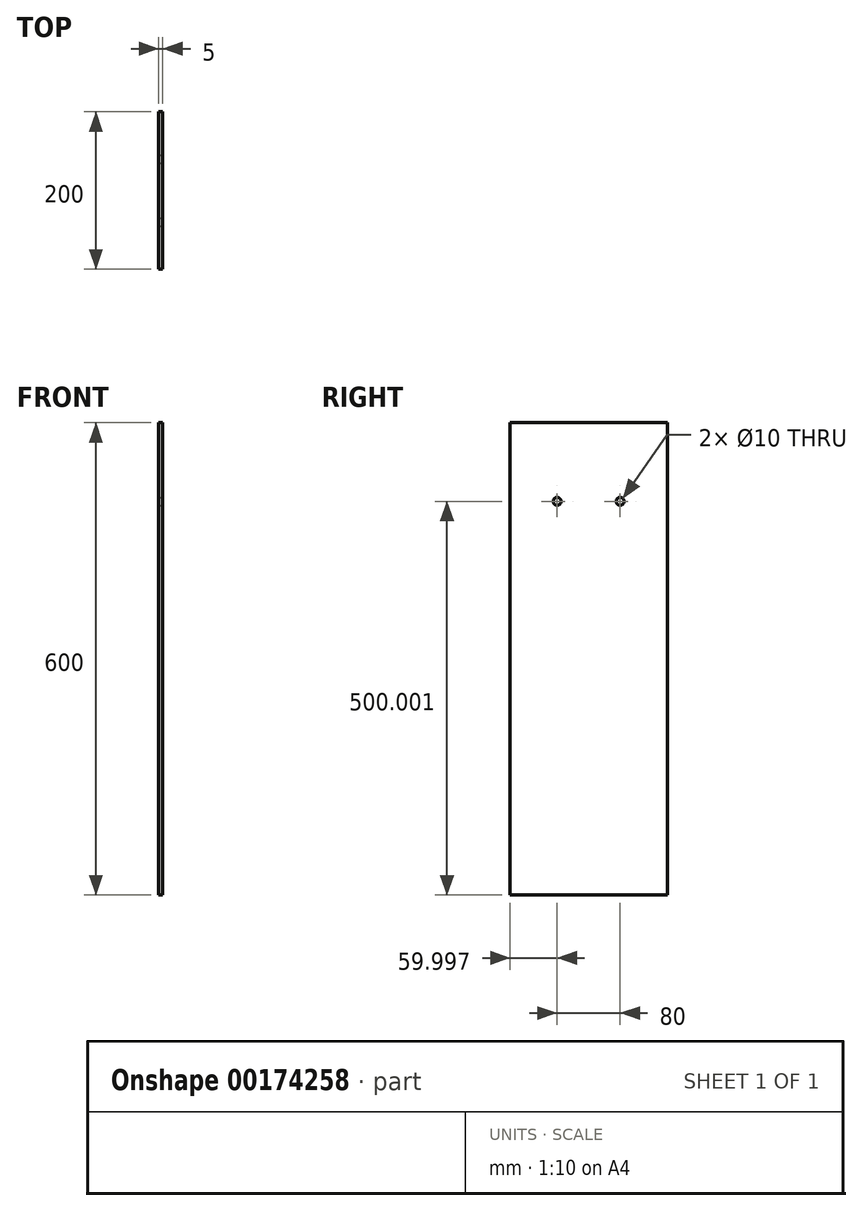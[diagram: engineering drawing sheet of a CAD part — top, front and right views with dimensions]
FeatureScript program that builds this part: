
annotation { "Feature Type Name" : "Feature", "Feature Type Description" : "" }
export const myFeature = defineFeature(function(context is Context, id is Id, definition is map)
    precondition{}
    {
        {
            var Q0;
            Q0=qCreatedBy(makeId("Right.planeOp"),FACE);
            var sketch = newSketch(context, id + "F0", { "sketchPlane" : qUnion([Q0])});
            skLineSegment(sketch, "E0.bottom", {"start": v(95.7, 383.9) * mm, "end": v(-104.3, 383.9) * mm});
            skLineSegment(sketch, "E0.top", {"start": v(95.7, -216.1) * mm, "end": v(-104.3, -216.1) * mm});
            skLineSegment(sketch, "E0.left", {"start": v(95.7, 383.9) * mm, "end": v(95.7, -216.1) * mm});
            skLineSegment(sketch, "E0.right", {"start": v(-104.3, 383.9) * mm, "end": v(-104.3, -216.1) * mm});
            skSolve(sketch);
        }
        {
            var Q0;
            Q0=makeQuery(id+"F0.imprint","IMPRINT",FACE,{"disambiguationData":[TD([[makeQuery(id+"F0.imprint","IMPRINT",EDGE,{"derivedFrom":sQuery(id+"F0.wireOp",EDGE,"E0.bottom")}),1.0]])]});
            extrude(context, id + "F1", {"entities" : qUnion([Q0]), "depth" : 5 * mm});
        }
        {
            var Q0;
            Q0=makeQuery(id+"F1.opExtrude","CAP_FACE",FACE,{"disambiguationData":[OSD([sQuery(id+"F0.wireOp",EDGE,"E0.bottom"),sQuery(id+"F0.wireOp",EDGE,"E0.top"),sQuery(id+"F0.wireOp",EDGE,"E0.left"),sQuery(id+"F0.wireOp",EDGE,"E0.right")])],"isStart":false});
            var sketch = newSketch(context, id + "F2", { "sketchPlane" : qUnion([Q0])});
            skSolve(sketch);
        }
        {
            var Q0;
            Q0=makeQuery(id+"F2.imprint","IMPRINT",FACE,{"disambiguationData":[TD([[makeQuery(id+"F2.imprint","IMPRINT",EDGE,{"derivedFrom":makeQuery(id+"F1.opExtrude","CAP_EDGE",EDGE,{"disambiguationData":[OSD([sQuery(id+"F0.wireOp",EDGE,"E0.bottom")])],"isStart":false})}),1.0]])]});
            var sketch = newSketch(context, id + "F3", { "sketchPlane" : qUnion([Q0])});
            skPoint(sketch, "E1", {"position": v(-44.3, 283.9) * mm});
            skPoint(sketch, "E2", {"position": v(35.7, 283.9) * mm});
            skSolve(sketch);
        }
        {
            var Q0;
            Q0=sQuery(id+"F3.wireOp",VERTEX,"E1");
            var Q1;
            Q1=sQuery(id+"F3.wireOp",VERTEX,"E2");
            var Q2;
            Q2=makeQuery(id+"F1.opExtrude","SWEPT_BODY",BODY,{"disambiguationData":[OSD([sQuery(id+"F0.wireOp",EDGE,"E0.bottom"),sQuery(id+"F0.wireOp",EDGE,"E0.top"),sQuery(id+"F0.wireOp",EDGE,"E0.left"),sQuery(id+"F0.wireOp",EDGE,"E0.right")])]});
            hole(context, id + "F4", {"style" : HoleStyle.SIMPLE, "endStyle" : HoleEndStyle.THROUGH, "holeDiameter" : 10 * mm, "locations" : qUnion([Q0, Q1]), "scope" : qUnion([Q2]), "isTappedThrough" : true});
        }
    });
